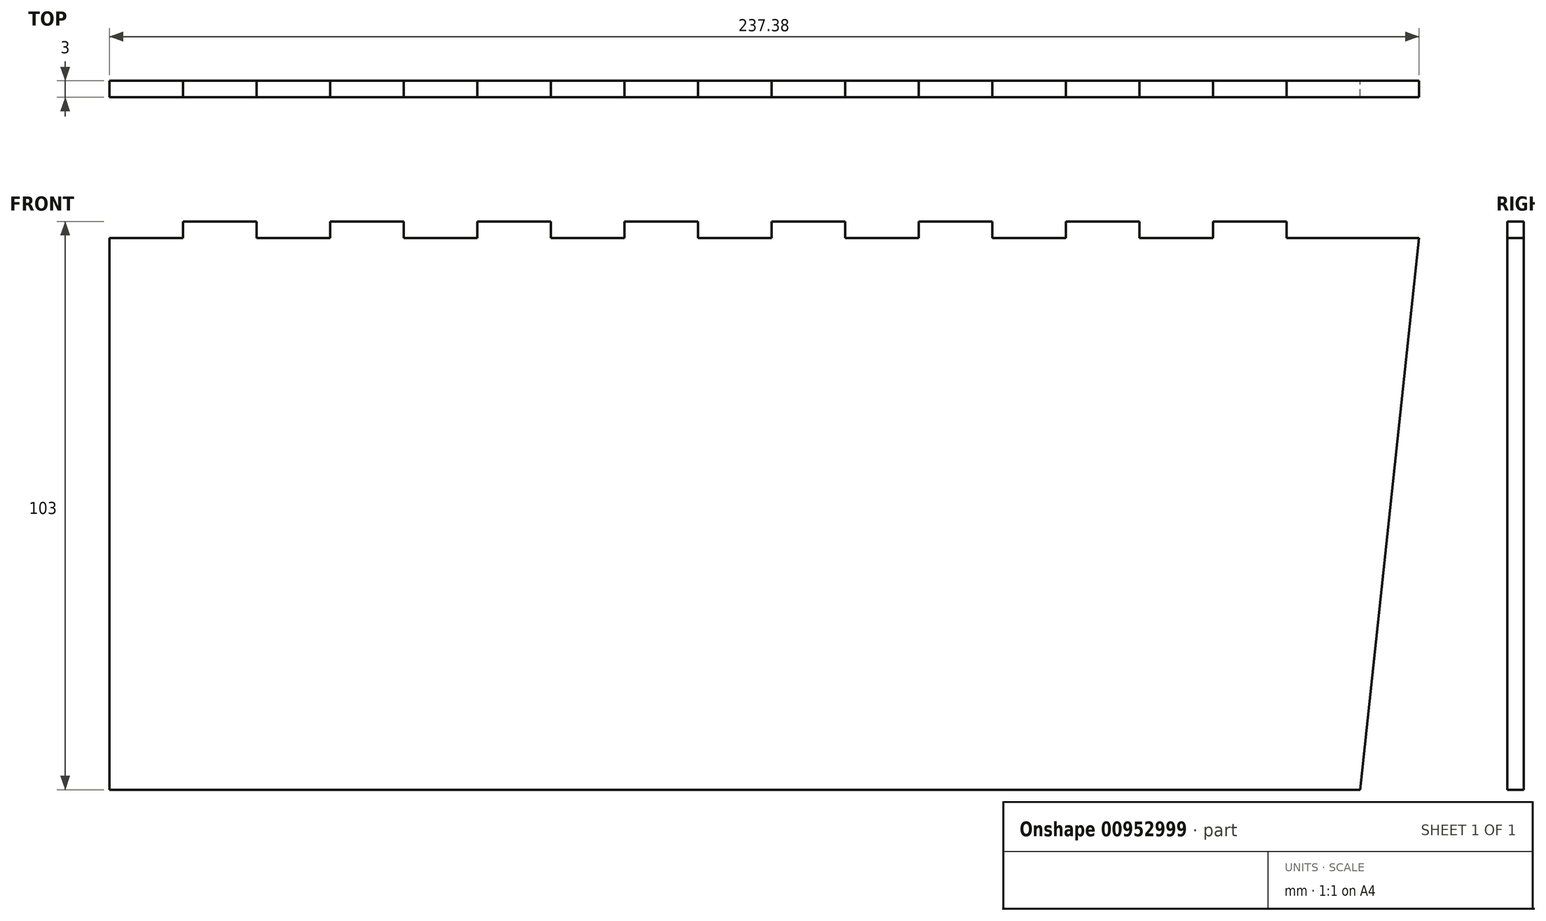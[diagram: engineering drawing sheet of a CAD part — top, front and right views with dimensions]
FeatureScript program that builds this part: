
annotation { "Feature Type Name" : "Feature", "Feature Type Description" : "" }
export const myFeature = defineFeature(function(context is Context, id is Id, definition is map)
    precondition{}
    {
        {
            var Q0;
            Q0=qCreatedBy(makeId("Front.planeOp"),FACE);
            var sketch = newSketch(context, id + "F0", { "sketchPlane" : qUnion([Q0])});
            skPoint(sketch, "E0.middle", {"position": v(0, 0) * mm});
            skLineSegment(sketch, "E1", {"start": v(-100, 50) * mm, "end": v(-86.67, 50) * mm});
            skLineSegment(sketch, "E2", {"start": v(-86.67, 50) * mm, "end": v(-86.67, 53) * mm});
            skLineSegment(sketch, "E3", {"start": v(-86.67, 53) * mm, "end": v(-73.33, 53) * mm});
            skLineSegment(sketch, "E4", {"start": v(-73.33, 53) * mm, "end": v(-73.33, 50) * mm});
            skLineSegment(sketch, "E5", {"start": v(-73.33, 50) * mm, "end": v(-60, 50) * mm});
            skLineSegment(sketch, "E6.1.0.1", {"start": v(-46.67, 50) * mm, "end": v(-33.33, 50) * mm});
            skLineSegment(sketch, "E6.1.0.2", {"start": v(-60, 53) * mm, "end": v(-46.67, 53) * mm});
            skLineSegment(sketch, "E6.1.0.3", {"start": v(-46.67, 53) * mm, "end": v(-46.67, 50) * mm});
            skLineSegment(sketch, "E6.1.0.4", {"start": v(-60, 50) * mm, "end": v(-60, 53) * mm});
            skLineSegment(sketch, "E6.2.0.0", {"start": v(-46.67, 50) * mm, "end": v(-33.33, 50) * mm});
            skLineSegment(sketch, "E6.2.0.1", {"start": v(-20, 50) * mm, "end": v(-6.67, 50) * mm});
            skLineSegment(sketch, "E6.2.0.2", {"start": v(-33.33, 53) * mm, "end": v(-20, 53) * mm});
            skLineSegment(sketch, "E6.2.0.3", {"start": v(-20, 53) * mm, "end": v(-20, 50) * mm});
            skLineSegment(sketch, "E6.2.0.4", {"start": v(-33.33, 50) * mm, "end": v(-33.33, 53) * mm});
            skLineSegment(sketch, "E6.3.0.0", {"start": v(-20, 50) * mm, "end": v(-6.67, 50) * mm});
            skLineSegment(sketch, "E6.3.0.1", {"start": v(6.67, 50) * mm, "end": v(20, 50) * mm});
            skLineSegment(sketch, "E6.3.0.2", {"start": v(-6.67, 53) * mm, "end": v(6.67, 53) * mm});
            skLineSegment(sketch, "E6.3.0.3", {"start": v(6.67, 53) * mm, "end": v(6.67, 50) * mm});
            skLineSegment(sketch, "E6.3.0.4", {"start": v(-6.67, 50) * mm, "end": v(-6.67, 53) * mm});
            skLineSegment(sketch, "E6.4.0.0", {"start": v(6.67, 50) * mm, "end": v(20, 50) * mm});
            skLineSegment(sketch, "E6.4.0.1", {"start": v(33.33, 50) * mm, "end": v(46.67, 50) * mm});
            skLineSegment(sketch, "E6.4.0.2", {"start": v(20, 53) * mm, "end": v(33.33, 53) * mm});
            skLineSegment(sketch, "E6.4.0.3", {"start": v(33.33, 53) * mm, "end": v(33.33, 50) * mm});
            skLineSegment(sketch, "E6.4.0.4", {"start": v(20, 50) * mm, "end": v(20, 53) * mm});
            skLineSegment(sketch, "E6.5.0.0", {"start": v(33.33, 50) * mm, "end": v(46.67, 50) * mm});
            skLineSegment(sketch, "E6.5.0.1", {"start": v(60, 50) * mm, "end": v(73.33, 50) * mm});
            skLineSegment(sketch, "E6.5.0.2", {"start": v(46.67, 53) * mm, "end": v(60, 53) * mm});
            skLineSegment(sketch, "E6.5.0.3", {"start": v(60, 53) * mm, "end": v(60, 50) * mm});
            skLineSegment(sketch, "E6.5.0.4", {"start": v(46.67, 50) * mm, "end": v(46.67, 53) * mm});
            skLineSegment(sketch, "E6.6.0.0", {"start": v(60, 50) * mm, "end": v(73.33, 50) * mm});
            skLineSegment(sketch, "E6.6.0.2", {"start": v(73.33, 53) * mm, "end": v(86.67, 53) * mm});
            skLineSegment(sketch, "E6.6.0.3", {"start": v(86.67, 53) * mm, "end": v(86.67, 50) * mm});
            skLineSegment(sketch, "E6.6.0.4", {"start": v(73.33, 50) * mm, "end": v(73.33, 53) * mm});
            skLineSegment(sketch, "E6.direction1", {"start": v(-100, 50) * mm, "end": v(-86.67, 50) * mm, "construction": true});
            skLineSegment(sketch, "E7", {"start": v(110.67, 50) * mm, "end": v(100, -50) * mm});
            skLineSegment(sketch, "E8", {"start": v(86.67, 50) * mm, "end": v(110.67, 50) * mm});
            skLineSegment(sketch, "E9", {"start": v(-126.7, 50) * mm, "end": v(-113.37, 50) * mm});
            skLineSegment(sketch, "E10", {"start": v(-113.37, 50) * mm, "end": v(-113.37, 53) * mm});
            skLineSegment(sketch, "E11.direction1", {"start": v(-126.7, 50) * mm, "end": v(-113.37, 50) * mm, "construction": true});
            skLineSegment(sketch, "E12", {"start": v(-126.7, -50) * mm, "end": v(100, -50) * mm});
            skLineSegment(sketch, "E13", {"start": v(-126.7, 50) * mm, "end": v(-126.7, -50) * mm});
            skLineSegment(sketch, "E14", {"start": v(-113.37, 53) * mm, "end": v(-100, 53) * mm});
            skLineSegment(sketch, "E15", {"start": v(-100, 53) * mm, "end": v(-100, 50) * mm});
            skSolve(sketch);
        }
        {
            var Q0;
            Q0=makeQuery(id+"F0.imprint","IMPRINT",FACE,{"disambiguationData":[TD([[makeQuery(id+"F0.imprint","IMPRINT",EDGE,{"derivedFrom":sQuery(id+"F0.wireOp",EDGE,"E1")}),-1.0]])]});
            extrude(context, id + "F1", {"entities" : qUnion([Q0]), "depth" : 3 * mm, "offsetDistance" : 25 * mm});
        }
    });
